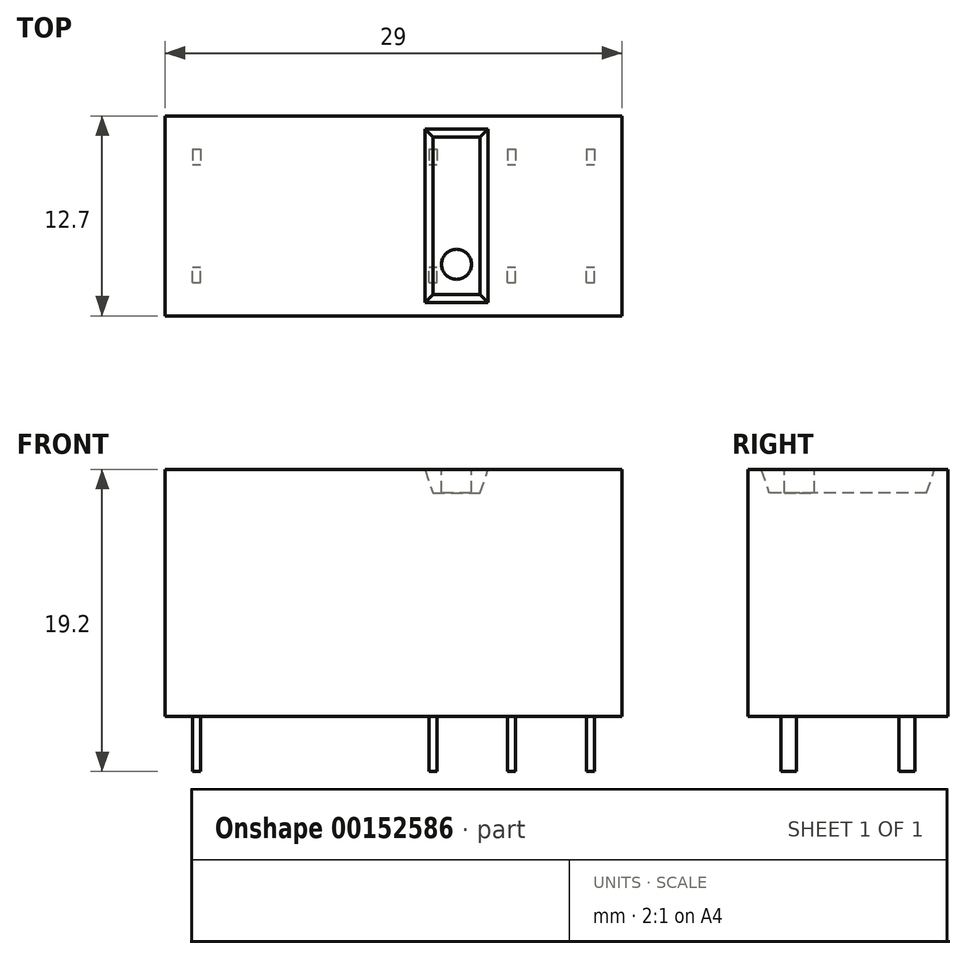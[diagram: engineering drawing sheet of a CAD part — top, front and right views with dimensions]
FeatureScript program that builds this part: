
annotation { "Feature Type Name" : "Feature", "Feature Type Description" : "" }
export const myFeature = defineFeature(function(context is Context, id is Id, definition is map)
    precondition{}
    {
        {
            var Q0;
            Q0=qCreatedBy(makeId("Right.planeOp"),FACE);
            var sketch = newSketch(context, id + "F0", { "sketchPlane" : qUnion([Q0])});
            skLineSegment(sketch, "E0.bottom", {"start": v(6.35, 15.7) * mm, "end": v(-6.35, 15.7) * mm});
            skLineSegment(sketch, "E0.top", {"start": v(6.35, 0) * mm, "end": v(-6.35, 0) * mm});
            skLineSegment(sketch, "E0.left", {"start": v(6.35, 15.7) * mm, "end": v(6.35, 0) * mm});
            skLineSegment(sketch, "E0.right", {"start": v(-6.35, 15.7) * mm, "end": v(-6.35, 0) * mm});
            skSolve(sketch);
        }
        {
            var Q0;
            Q0 = qSketchRegion(id + "F0", true);
            extrude(context, id + "F1", {"entities" : qUnion([Q0]), "endBound" : BoundingType.SYMMETRIC, "depth" : 29 * mm});
        }
        {
            var Q0;
            Q0=qCreatedBy(makeId("Top.planeOp"),FACE);
            var sketch = newSketch(context, id + "F2", { "sketchPlane" : qUnion([Q0])});
            skLineSegment(sketch, "E1.bottom", {"start": v(-12.75, 4.25) * mm, "end": v(-12.25, 4.25) * mm});
            skLineSegment(sketch, "E1.top", {"start": v(-12.75, 3.25) * mm, "end": v(-12.25, 3.25) * mm});
            skLineSegment(sketch, "E1.left", {"start": v(-12.75, 4.25) * mm, "end": v(-12.75, 3.25) * mm});
            skLineSegment(sketch, "E1.right", {"start": v(-12.25, 4.25) * mm, "end": v(-12.25, 3.25) * mm});
            skPoint(sketch, "E2.endSnap0", {"position": v(-12.25, 3.75) * mm});
            skPoint(sketch, "E3", {"position": v(-12.5, 3.25) * mm});
            skLineSegment(sketch, "E4.bottom", {"start": v(2.25, 4.25) * mm, "end": v(2.75, 4.25) * mm});
            skLineSegment(sketch, "E4.top", {"start": v(2.25, 3.25) * mm, "end": v(2.75, 3.25) * mm});
            skLineSegment(sketch, "E4.left", {"start": v(2.25, 4.25) * mm, "end": v(2.25, 3.25) * mm});
            skLineSegment(sketch, "E4.right", {"start": v(2.75, 4.25) * mm, "end": v(2.75, 3.25) * mm});
            skPoint(sketch, "E5.endSnap0", {"position": v(2.75, 3.75) * mm});
            skPoint(sketch, "E6", {"position": v(2.5, 3.25) * mm});
            skLineSegment(sketch, "E7.bottom", {"start": v(7.25, 4.25) * mm, "end": v(7.75, 4.25) * mm});
            skLineSegment(sketch, "E7.top", {"start": v(7.25, 3.25) * mm, "end": v(7.75, 3.25) * mm});
            skLineSegment(sketch, "E7.left", {"start": v(7.25, 4.25) * mm, "end": v(7.25, 3.25) * mm});
            skLineSegment(sketch, "E7.right", {"start": v(7.75, 4.25) * mm, "end": v(7.75, 3.25) * mm});
            skPoint(sketch, "E8.endSnap0", {"position": v(7.75, 3.75) * mm});
            skPoint(sketch, "E9", {"position": v(7.5, 3.25) * mm});
            skLineSegment(sketch, "E10.bottom", {"start": v(12.25, 4.25) * mm, "end": v(12.75, 4.25) * mm});
            skLineSegment(sketch, "E10.top", {"start": v(12.25, 3.25) * mm, "end": v(12.75, 3.25) * mm});
            skLineSegment(sketch, "E10.left", {"start": v(12.25, 4.25) * mm, "end": v(12.25, 3.25) * mm});
            skLineSegment(sketch, "E10.right", {"start": v(12.75, 4.25) * mm, "end": v(12.75, 3.25) * mm});
            skPoint(sketch, "E11.endSnap0", {"position": v(12.75, 3.75) * mm});
            skPoint(sketch, "E12", {"position": v(12.5, 3.25) * mm});
            skLineSegment(sketch, "E13.MirrorCS", {"start": v(2.75, -4.25) * mm, "end": v(2.75, -3.25) * mm});
            skLineSegment(sketch, "E14.MirrorCS", {"start": v(7.25, -4.25) * mm, "end": v(7.75, -4.25) * mm});
            skLineSegment(sketch, "E15.MirrorCS", {"start": v(7.25, -3.25) * mm, "end": v(7.75, -3.25) * mm});
            skLineSegment(sketch, "E16.MirrorCS", {"start": v(7.75, -4.25) * mm, "end": v(7.75, -3.25) * mm});
            skLineSegment(sketch, "E17.MirrorCS", {"start": v(12.25, -4.25) * mm, "end": v(12.75, -4.25) * mm});
            skLineSegment(sketch, "E18.MirrorCS", {"start": v(2.25, -3.25) * mm, "end": v(2.75, -3.25) * mm});
            skLineSegment(sketch, "E19.MirrorCS", {"start": v(2.25, -4.25) * mm, "end": v(2.75, -4.25) * mm});
            skLineSegment(sketch, "E20.MirrorCS", {"start": v(-12.25, -4.25) * mm, "end": v(-12.25, -3.25) * mm});
            skLineSegment(sketch, "E21.MirrorCS", {"start": v(-12.75, -3.25) * mm, "end": v(-12.25, -3.25) * mm});
            skLineSegment(sketch, "E22.MirrorCS", {"start": v(-12.75, -4.25) * mm, "end": v(-12.25, -4.25) * mm});
            skLineSegment(sketch, "E23.MirrorCS", {"start": v(12.75, -4.25) * mm, "end": v(12.75, -3.25) * mm});
            skLineSegment(sketch, "E24.MirrorCS", {"start": v(12.25, -3.25) * mm, "end": v(12.75, -3.25) * mm});
            skPoint(sketch, "E25.MirrorP", {"position": v(-12.25, -3.75) * mm});
            skPoint(sketch, "E26.MirrorP", {"position": v(7.75, -3.75) * mm});
            skPoint(sketch, "E27.MirrorP", {"position": v(12.75, -3.75) * mm});
            skPoint(sketch, "E28.MirrorP", {"position": v(2.75, -3.75) * mm});
            skLineSegment(sketch, "E29.MirrorCS", {"start": v(7.25, -4.25) * mm, "end": v(7.25, -3.25) * mm});
            skPoint(sketch, "E30.MirrorP", {"position": v(12.5, -3.25) * mm});
            skPoint(sketch, "E31.MirrorP", {"position": v(2.5, -3.25) * mm});
            skLineSegment(sketch, "E32.MirrorCS", {"start": v(2.25, -4.25) * mm, "end": v(2.25, -3.25) * mm});
            skLineSegment(sketch, "E33.MirrorCS", {"start": v(12.25, -4.25) * mm, "end": v(12.25, -3.25) * mm});
            skLineSegment(sketch, "E34.MirrorCS", {"start": v(-12.75, -4.25) * mm, "end": v(-12.75, -3.25) * mm});
            skPoint(sketch, "E35.MirrorP", {"position": v(-12.5, -3.25) * mm});
            skPoint(sketch, "E36.MirrorP", {"position": v(7.5, -3.25) * mm});
            skSolve(sketch);
        }
        {
            var Q0;
            Q0 = qSketchRegion(id + "F2", true);
            extrude(context, id + "F3", {"entities" : qUnion([Q0]), "operationType" : NewBodyOperationType.ADD, "oppositeDirection" : true, "depth" : 3.5 * mm});
        }
        {
            var Q0;
            Q0=makeQuery(id+"F1.opExtrude","SWEPT_FACE",FACE,{"disambiguationData":[OSD([sQuery(id+"F0.wireOp",EDGE,"E0.bottom")])]});
            var sketch = newSketch(context, id + "F4", { "sketchPlane" : qUnion([Q0])});
            skLineSegment(sketch, "E37.bottom", {"start": v(2, 5.5) * mm, "end": v(6, 5.5) * mm});
            skLineSegment(sketch, "E37.top", {"start": v(2, -5.5) * mm, "end": v(6, -5.5) * mm});
            skLineSegment(sketch, "E37.left", {"start": v(2, 5.5) * mm, "end": v(2, -5.5) * mm});
            skLineSegment(sketch, "E37.right", {"start": v(6, 5.5) * mm, "end": v(6, -5.5) * mm});
            skPoint(sketch, "E38", {"position": v(2, 0) * mm});
            skCircle(sketch, "E39", {"center": v(4, -3.08) * mm, "radius": 0.95 * mm});
            skPoint(sketch, "E40", {"position": v(4, -5.5) * mm});
            skSolve(sketch);
        }
        {
            var Q0;
            Q0 = qSketchRegion(id + "F4", true);
            extrude(context, id + "F5", {"entities" : qUnion([Q0]), "operationType" : NewBodyOperationType.REMOVE, "oppositeDirection" : true, "depth" : 1.5 * mm});
        }
        {
            var Q0;
            Q0=makeQuery(id+"F5.boolean.opBoolean","COPY",EDGE,{"derivedFrom":makeQuery(id+"F5.opExtrude","CAP_EDGE",EDGE,{"disambiguationData":[OSD([sQuery(id+"F4.wireOp",EDGE,"E37.left")])],"isStart":false})});
            var Q1;
            Q1=makeQuery(id+"F5.boolean.opBoolean","COPY",EDGE,{"derivedFrom":makeQuery(id+"F5.opExtrude","CAP_EDGE",EDGE,{"disambiguationData":[OSD([sQuery(id+"F4.wireOp",EDGE,"E37.bottom")])],"isStart":false})});
            var Q2;
            Q2=makeQuery(id+"F5.boolean.opBoolean","COPY",EDGE,{"derivedFrom":makeQuery(id+"F5.opExtrude","CAP_EDGE",EDGE,{"disambiguationData":[OSD([sQuery(id+"F4.wireOp",EDGE,"E37.right")])],"isStart":false})});
            var Q3;
            Q3=makeQuery(id+"F5.boolean.opBoolean","COPY",EDGE,{"derivedFrom":makeQuery(id+"F5.opExtrude","CAP_EDGE",EDGE,{"disambiguationData":[OSD([sQuery(id+"F4.wireOp",EDGE,"E37.top")])],"isStart":false})});
            chamfer(context, id + "F6", {"entities" : qUnion([Q0, Q1, Q2, Q3]), "chamferType" : ChamferType.TWO_OFFSETS, "width1" : 0.5 * mm, "oppositeDirection" : false, "width2" : 1.5 * mm, "tangentPropagation" : true});
        }
    });
